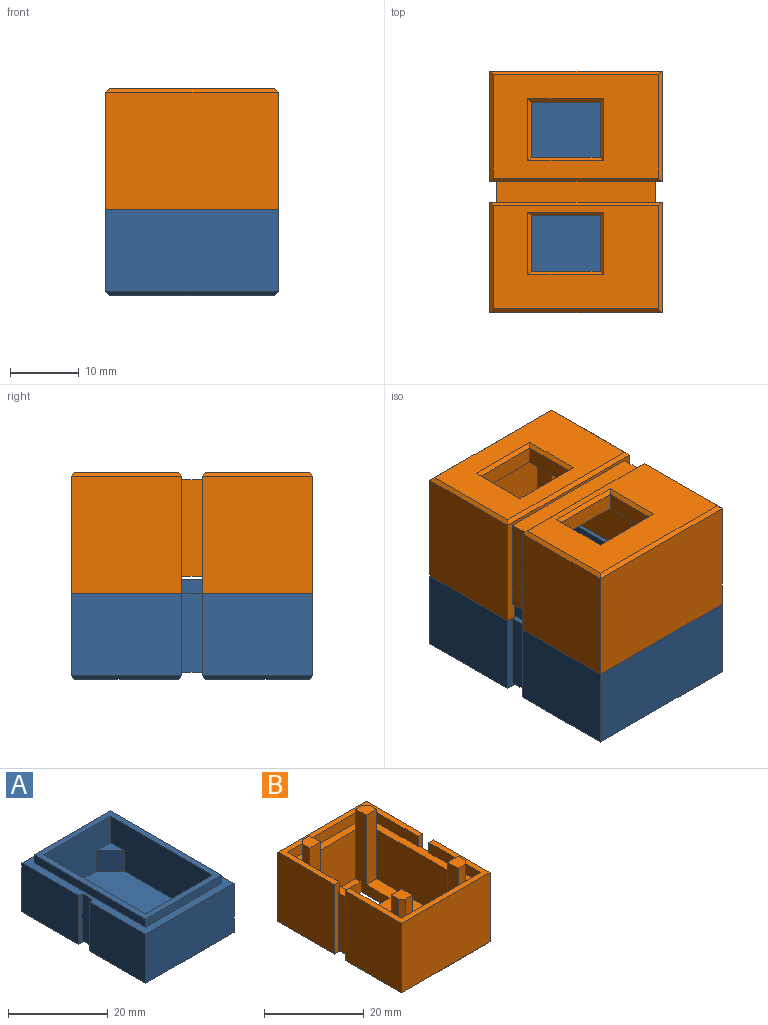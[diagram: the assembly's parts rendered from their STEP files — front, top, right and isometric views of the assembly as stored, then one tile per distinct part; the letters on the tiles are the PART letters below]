
ASSEMBLY  parts=2 mates=1
PART A: 40 faces, bbox 25x35x14.5 mm
  f0: plane 16x12mm, normal (-1,0,0), area 192mm2, adj f2,f7,f29,f33
  f1: plane 16x12mm, normal (1,0,0), area 192mm2, adj f2,f7,f29,f34
  f2: plane 35x25mm, normal (0,0,1), area 186.4mm2, adj f0,f1,f5,f6,f7,f8,f10,f11
  f3: plane 23x3mm, normal (0,0,-1), area 69mm2, adj f28,f29,f30,f31
  f4: plane 24x15mm, normal (0,0,-1), area 360mm2, adj f36,f37,f38,f39
  f5: plane 25x12mm, normal (0,1,0), area 300mm2, adj f2,f6,f8,f36
  f6: plane 16x12mm, normal (-1,0,0), area 192mm2, adj f2,f5,f28,f37
  f7: plane 25x12mm, normal (0,-1,0), area 300mm2, adj f0,f1,f2,f32
  f8: plane 16x12mm, normal (1,0,0), area 192mm2, adj f2,f5,f28,f38
  f9: plane 24x15mm, normal (0,0,-1), area 360mm2, adj f32,f33,f34,f35
  f10: plane 21.6x2mm, normal (0,1,0), area 43.2mm2, adj f2,f11,f13,f14
  f11: plane 31.6x2mm, normal (-1,0,0), area 63.2mm2, adj f2,f10,f12,f14
  f12: plane 21.6x2mm, normal (0,-1,0), area 43.2mm2, adj f2,f11,f13,f14
  f13: plane 31.6x2mm, normal (1,0,0), area 63.2mm2, adj f2,f10,f12,f14
  f14: plane 31.6x21.6mm, normal (0,0,1), area 131.6mm2, adj f10,f11,f12,f13,f24,f25,f26,f27
  f15: plane 5x4mm, normal (-0.71,0.71,0), area 28.3mm2, adj f16,f19,f26,f27
  f16: plane 4x4mm, normal (0,0,1), area 8mm2, adj f15,f26,f27
  f17: plane 5x4mm, normal (0.71,0.71,0), area 28.3mm2, adj f18,f19,f25,f26
  f18: plane 4x4mm, normal (0,0,1), area 8mm2, adj f17,f25,f26
  f19: plane 29x19mm, normal (0,0,1), area 519mm2, adj f15,f17,f20,f23,f24,f25,f26,f27
  f20: plane 5x4mm, normal (0.71,-0.71,0), area 28.3mm2, adj f19,f21,f24,f25
  f21: plane 4x4mm, normal (0,0,1), area 8mm2, adj f20,f24,f25
  f22: plane 4x4mm, normal (0,0,1), area 8mm2, adj f23,f24,f27
  f23: plane 5x4mm, normal (-0.71,-0.71,0), area 28.3mm2, adj f19,f22,f24,f27
  f24: plane 19x11.5mm, normal (0,-1,0), area 178.5mm2, adj f14,f19,f20,f21,f22,f23,f25,f27
  f25: plane 29x11.5mm, normal (1,0,0), area 293.5mm2, adj f14,f17,f18,f19,f20,f21,f24,f26
  f26: plane 19x11.5mm, normal (0,1,0), area 178.5mm2, adj f14,f15,f16,f17,f18,f19,f25,f27
  f27: plane 29x11.5mm, normal (-1,0,0), area 293.5mm2, adj f14,f15,f16,f19,f22,f23,f24,f26
  f28: plane 25x12mm, normal (0,-1,0), area 35.5mm2, adj f2,f3,f6,f8,f30,f31,f39
  f29: plane 25x12mm, normal (0,1,0), area 35.5mm2, adj f0,f1,f2,f3,f30,f31,f35
  f30: plane 11.5x3mm, normal (-1,0,0), area 34.5mm2, adj f2,f3,f28,f29
  f31: plane 11.5x3mm, normal (1,0,0), area 34.5mm2, adj f2,f3,f28,f29
  f32: plane 25x0.5mm, normal (0,-0.71,-0.71), area 17.3mm2, adj f7,f9,f33,f34
  f33: plane 16x0.5mm, normal (-0.71,0,-0.71), area 11mm2, adj f0,f9,f32,f35
  f34: plane 16x0.5mm, normal (0.71,0,-0.71), area 11mm2, adj f1,f9,f32,f35
  f35: plane 25x0.5mm, normal (0,0.71,-0.71), area 17.3mm2, adj f9,f29,f33,f34
  f36: plane 25x0.5mm, normal (0,0.71,-0.71), area 17.3mm2, adj f4,f5,f37,f38
  f37: plane 16x0.5mm, normal (-0.71,0,-0.71), area 11mm2, adj f4,f6,f36,f39
  f38: plane 16x0.5mm, normal (0.71,0,-0.71), area 11mm2, adj f4,f8,f36,f39
  f39: plane 25x0.5mm, normal (0,-0.71,-0.71), area 17.3mm2, adj f4,f28,f37,f38
PART B: 74 faces, bbox 25x35x20 mm
  f0: plane 23x12mm, normal (-1,0,0), area 276mm2, adj f1,f7,f53,f67
  f1: plane 29x19mm, normal (0,0,1), area 355mm2, adj f0,f2,f3,f4,f26,f27,f28,f29
  f2: plane 13x12mm, normal (0,1,0), area 156mm2, adj f1,f7,f61,f68
  f3: plane 23x12mm, normal (1,0,0), area 276mm2, adj f1,f7,f58,f62
  f4: plane 13x12mm, normal (0,-1,0), area 156mm2, adj f1,f7,f27,f55
  f5: plane 24x15mm, normal (0,0,-1), area 261mm2, adj f35,f36,f37,f38,f39,f40,f41,f42
  f6: plane 14x3mm, normal (-1,0,0), area 42mm2, adj f7,f12,f14,f34
  f7: plane 32.4x23mm, normal (0,0,1), area 178.6mm2, adj f0,f2,f3,f4,f6,f12,f13,f14
  f8: plane 17x16mm, normal (-1,0,0), area 272mm2, adj f14,f16,f21,f36
  f9: plane 17x16mm, normal (-1,0,0), area 272mm2, adj f10,f12,f25,f44
  f10: plane 25x17mm, normal (0,-1,0), area 425mm2, adj f9,f11,f25,f43
  f11: plane 17x16mm, normal (1,0,0), area 272mm2, adj f10,f12,f25,f45
  f12: plane 25x17mm, normal (0,1,0), area 47mm2, adj f6,f7,f9,f11,f13,f22,f24,f25
  f13: plane 14x3mm, normal (1,0,0), area 42mm2, adj f7,f12,f14,f34
  f14: plane 25x17mm, normal (0,-1,0), area 47mm2, adj f6,f7,f8,f13,f15,f18,f20,f21
  f15: plane 17x16mm, normal (1,0,0), area 272mm2, adj f14,f16,f21,f37
  f16: plane 25x17mm, normal (0,1,0), area 425mm2, adj f8,f15,f21,f35
  f17: plane 24x15mm, normal (0,0,-1), area 261mm2, adj f43,f44,f45,f46,f47,f48,f49,f50
  f18: plane 14.7x2.5mm, normal (1,0,0), area 36.8mm2, adj f7,f14,f19,f21
  f19: plane 22.4x2.5mm, normal (0,-1,0), area 56mm2, adj f7,f18,f20,f21
  f20: plane 14.7x2.5mm, normal (-1,0,0), area 36.8mm2, adj f7,f14,f19,f21
  f21: plane 25x16mm, normal (0,0,1), area 70.7mm2, adj f8,f14,f15,f16,f18,f19,f20
  f22: plane 14.7x2.5mm, normal (-1,0,0), area 36.8mm2, adj f7,f12,f23,f25
  f23: plane 22.4x2.5mm, normal (0,1,0), area 56mm2, adj f7,f22,f24,f25
  f24: plane 14.7x2.5mm, normal (1,0,0), area 36.8mm2, adj f7,f12,f23,f25
  f25: plane 25x16mm, normal (0,0,1), area 70.7mm2, adj f9,f10,f11,f12,f22,f23,f24
  f26: plane 10x2.5mm, normal (0,-1,0), area 25mm2, adj f1,f27,f28,f41
  f27: plane 19.5x9.5mm, normal (-1,0,0), area 71mm2, adj f1,f4,f26,f29,f39,f52,f53,f54
  f28: plane 8x2.5mm, normal (1,0,0), area 20mm2, adj f1,f26,f29,f42
  f29: plane 10x2.5mm, normal (0,1,0), area 25mm2, adj f1,f27,f28,f40
  f30: plane 10x2.5mm, normal (0,-1,0), area 25mm2, adj f1,f31,f32,f49
  f31: plane 8x2.5mm, normal (-1,0,0), area 20mm2, adj f1,f30,f33,f47
  f32: plane 8x2.5mm, normal (1,0,0), area 20mm2, adj f1,f30,f33,f50
  f33: plane 10x2.5mm, normal (0,1,0), area 25mm2, adj f1,f31,f32,f48
  f34: plane 23x3mm, normal (0,0,-1), area 69mm2, adj f6,f12,f13,f14
  f35: plane 25x0.5mm, normal (0,0.71,-0.71), area 17.3mm2, adj f5,f16,f36,f37
  f36: plane 16x0.5mm, normal (-0.71,0,-0.71), area 11mm2, adj f5,f8,f35,f38
  f37: plane 16x0.5mm, normal (0.71,0,-0.71), area 11mm2, adj f5,f15,f35,f38
  f38: plane 25x0.5mm, normal (0,-0.71,-0.71), area 17.3mm2, adj f5,f14,f36,f37
  f39: plane 9x0.5mm, normal (-0.71,0,-0.71), area 6mm2, adj f5,f27,f40,f41
  f40: plane 11x0.5mm, normal (0,0.71,-0.71), area 7.4mm2, adj f5,f29,f39,f42
  f41: plane 11x0.5mm, normal (0,-0.71,-0.71), area 7.4mm2, adj f5,f26,f39,f42
  f42: plane 9x0.5mm, normal (0.71,0,-0.71), area 6mm2, adj f5,f28,f40,f41
  f43: plane 25x0.5mm, normal (0,-0.71,-0.71), area 17.3mm2, adj f10,f17,f44,f45
  f44: plane 16x0.5mm, normal (-0.71,0,-0.71), area 11mm2, adj f9,f17,f43,f46
  f45: plane 16x0.5mm, normal (0.71,0,-0.71), area 11mm2, adj f11,f17,f43,f46
  f46: plane 25x0.5mm, normal (0,0.71,-0.71), area 17.3mm2, adj f12,f17,f44,f45
  f47: plane 9x0.5mm, normal (-0.71,0,-0.71), area 6mm2, adj f17,f31,f48,f49
  f48: plane 11x0.5mm, normal (0,0.71,-0.71), area 7.4mm2, adj f17,f33,f47,f50
  f49: plane 11x0.5mm, normal (0,-0.71,-0.71), area 7.4mm2, adj f17,f30,f47,f50
  f50: plane 9x0.5mm, normal (0.71,0,-0.71), area 6mm2, adj f17,f32,f48,f49
  f51: plane 5x2mm, normal (1,0,0), area 10mm2, adj f7,f53,f54,f73
  f52: plane 5x2mm, normal (0,1,0), area 10mm2, adj f7,f27,f54,f73
  f53: plane 17x3mm, normal (0,-1,0), area 51mm2, adj f0,f1,f27,f51,f54
  f54: plane 3x3mm, normal (0,0,1), area 8.5mm2, adj f27,f51,f52,f53,f73
  f55: plane 17x3mm, normal (1,0,0), area 51mm2, adj f1,f4,f56,f58,f59
  f56: plane 5x2mm, normal (0,1,0), area 10mm2, adj f7,f55,f59,f72
  f57: plane 5x2mm, normal (-1,0,0), area 10mm2, adj f7,f58,f59,f72
  f58: plane 17x3mm, normal (0,-1,0), area 51mm2, adj f1,f3,f55,f57,f59
  f59: plane 3x3mm, normal (0,0,1), area 8.5mm2, adj f55,f56,f57,f58,f72
  f60: plane 5x2mm, normal (0,-1,0), area 10mm2, adj f7,f61,f64,f71
  f61: plane 17x3mm, normal (1,0,0), area 51mm2, adj f1,f2,f60,f62,f64
  f62: plane 17x3mm, normal (0,1,0), area 51mm2, adj f1,f3,f61,f63,f64
  f63: plane 5x2mm, normal (-1,0,0), area 10mm2, adj f7,f62,f64,f71
  f64: plane 3x3mm, normal (0,0,1), area 8.5mm2, adj f60,f61,f62,f63,f71
  f65: plane 5x2mm, normal (0,-1,0), area 10mm2, adj f7,f68,f69,f70
  f66: plane 5x2mm, normal (1,0,0), area 10mm2, adj f7,f67,f69,f70
  f67: plane 17x3mm, normal (0,1,0), area 51mm2, adj f0,f1,f66,f68,f69
  f68: plane 17x3mm, normal (-1,0,0), area 51mm2, adj f1,f2,f65,f67,f69
  f69: plane 3x3mm, normal (0,0,1), area 8.5mm2, adj f65,f66,f67,f68,f70
  f70: plane 5x1mm, normal (0.71,-0.71,0), area 7.1mm2, adj f7,f65,f66,f69
  f71: plane 5x1mm, normal (-0.71,-0.71,0), area 7.1mm2, adj f7,f60,f63,f64
  f72: plane 5x1mm, normal (-0.71,0.71,0), area 7.1mm2, adj f7,f56,f57,f59
  f73: plane 5x1mm, normal (0.71,0.71,0), area 7.1mm2, adj f7,f51,f52,f54
PLACE A at identity fixed
PLACE B rot(axis=(0,1,0),180deg) t=(0,0,24)mm
MATE fastened B.f25 <-> A.f2  axis (0,0,-1) through (-12.5,-17.5,9.5)mm
